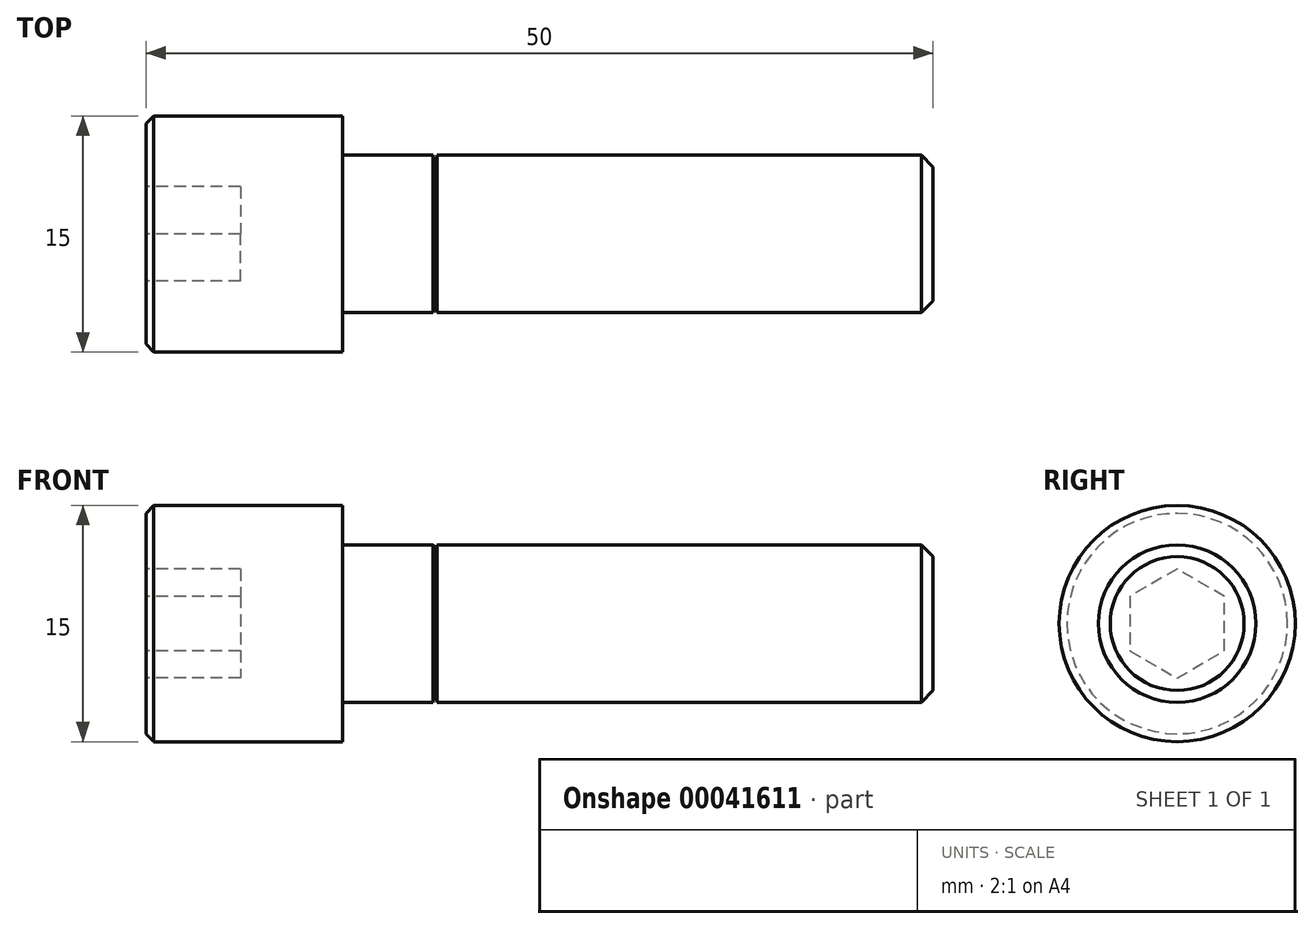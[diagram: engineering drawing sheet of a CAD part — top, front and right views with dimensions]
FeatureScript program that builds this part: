
annotation { "Feature Type Name" : "Feature", "Feature Type Description" : "" }
export const myFeature = defineFeature(function(context is Context, id is Id, definition is map)
    precondition{}
    {
        {
            var Q0;
            Q0=qCreatedBy(makeId("Front.planeOp"),FACE);
            var sketch = newSketch(context, id + "F0", { "sketchPlane" : qUnion([Q0])});
            skLineSegment(sketch, "E0.rect.bottom", {"start": v(12.5, 7.5) * mm, "end": v(0, 7.5) * mm});
            skLineSegment(sketch, "E0.rect.top", {"start": v(50, -7.5) * mm, "end": v(0, -7.5) * mm, "construction": true});
            skLineSegment(sketch, "E0.rect.left", {"start": v(50, 7.5) * mm, "end": v(50, -7.5) * mm, "construction": true});
            skLineSegment(sketch, "E0.rect.right", {"start": v(0, 7.5) * mm, "end": v(0, -7.5) * mm, "construction": true});
            skPoint(sketch, "E0.rect.middle", {"position": v(25, 0) * mm});
            skLineSegment(sketch, "E1", {"start": v(0, 0) * mm, "end": v(50, 0) * mm});
            skLineSegment(sketch, "E2", {"start": v(0, 7.5) * mm, "end": v(0, 0) * mm});
            skLineSegment(sketch, "E3", {"start": v(50, 4.25) * mm, "end": v(50, 0) * mm});
            skLineSegment(sketch, "E4", {"start": v(12.5, 7.5) * mm, "end": v(12.5, 5) * mm});
            skLineSegment(sketch, "E5", {"start": v(12.5, 5) * mm, "end": v(18.25, 5) * mm});
            skLineSegment(sketch, "E6", {"start": v(18.25, 5) * mm, "end": v(18.37, 4.25) * mm});
            skLineSegment(sketch, "E7", {"start": v(18.37, 4.25) * mm, "end": v(18.5, 5) * mm});
            skLineSegment(sketch, "E8", {"start": v(18.5, 5) * mm, "end": v(49.25, 5) * mm});
            skLineSegment(sketch, "E9", {"start": v(49.25, 5) * mm, "end": v(50, 4.25) * mm});
            skLineSegment(sketch, "E10", {"start": v(18.37, 4.25) * mm, "end": v(50, 4.25) * mm, "construction": true});
            skLineSegment(sketch, "E11", {"start": v(49.25, 5) * mm, "end": v(50, 5.75) * mm, "construction": true});
            skPoint(sketch, "E12", {"position": v(50, 4.25) * mm});
            skPoint(sketch, "E13", {"position": v(49.25, 5) * mm});
            skPoint(sketch, "E14", {"position": v(50, -4.25) * mm});
            skLineSegment(sketch, "E15", {"start": v(50, 0) * mm, "end": v(50, -4.25) * mm});
            skLineSegment(sketch, "E16", {"start": v(49.25, 5) * mm, "end": v(49.25, -5) * mm, "construction": true});
            skPoint(sketch, "E17", {"position": v(49.25, 0) * mm});
            skSolve(sketch);
        }
        {
            var Q0;
            Q0=makeQuery(id+"F0.imprint","IMPRINT",FACE,{"disambiguationData":[TD([[makeQuery(id+"F0.imprint","IMPRINT",EDGE,{"derivedFrom":sQuery(id+"F0.wireOp",EDGE,"E0.rect.bottom")}),1.0]])]});
            var Q1;
            Q1=sQuery(id+"F0.wireOp",EDGE,"E1");
            revolve(context, id + "F1", {"entities" : qUnion([Q0]), "axis" : qUnion([Q1]), "revolveType" : RevolveType.FULL});
        }
        {
            var Q0;
            Q0=makeQuery(id+"F1.opRevolve","SWEPT_EDGE",EDGE,{"disambiguationData":[OSD([sQuery(id+"F0.wireOp",EDGE,"E0.rect.bottom"),sQuery(id+"F0.wireOp",EDGE,"E2")])]});
            chamfer(context, id + "F2", {"entities" : qUnion([Q0]), "width" : 0.5 * mm, "tangentPropagation" : true});
        }
        {
            var Q0;
            Q0=makeQuery(id+"F1.opRevolve","SWEPT_FACE",FACE,{"disambiguationData":[OSD([sQuery(id+"F0.wireOp",EDGE,"E2")])]});
            var sketch = newSketch(context, id + "F3", { "sketchPlane" : qUnion([Q0])});
            skCircle(sketch, "E18.0", {"center": v(0, 0) * mm, "radius": 7.5 * mm});
            skCircle(sketch, "E19.cCircle", {"center": v(0, 0) * mm, "radius": 3.46 * mm, "construction": true});
            skLineSegment(sketch, "E19.0", {"start": v(3, -1.73) * mm, "end": v(0, -3.46) * mm});
            skLineSegment(sketch, "E19.1", {"start": v(0, -3.46) * mm, "end": v(-3, -1.73) * mm});
            skLineSegment(sketch, "E19.2", {"start": v(-3, -1.73) * mm, "end": v(-3, 1.73) * mm});
            skLineSegment(sketch, "E19.3", {"start": v(-3, 1.73) * mm, "end": v(0, 3.46) * mm});
            skLineSegment(sketch, "E19.4", {"start": v(0, 3.46) * mm, "end": v(3, 1.73) * mm});
            skLineSegment(sketch, "E19.5", {"start": v(3, 1.73) * mm, "end": v(3, -1.73) * mm});
            skSolve(sketch);
        }
        {
            var Q0;
            Q0=makeQuery(id+"F3.imprint","IMPRINT",FACE,{"disambiguationData":[TD([[makeQuery(id+"F3.imprint","IMPRINT",EDGE,{"derivedFrom":sQuery(id+"F3.wireOp",EDGE,"E19.0")}),-1.0]])]});
            extrude(context, id + "F4", {"entities" : qUnion([Q0]), "operationType" : NewBodyOperationType.REMOVE, "oppositeDirection" : true, "depth" : 6 * mm});
        }
    });
